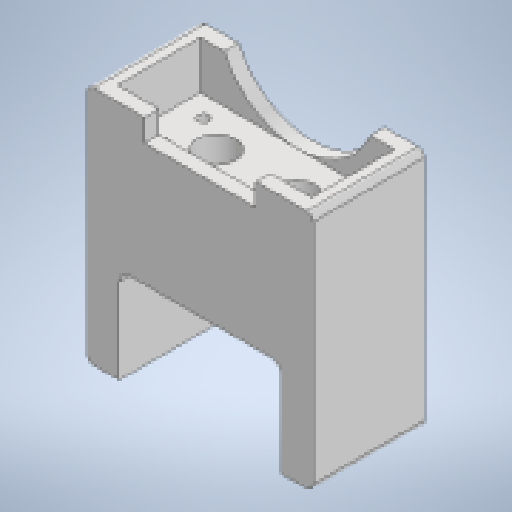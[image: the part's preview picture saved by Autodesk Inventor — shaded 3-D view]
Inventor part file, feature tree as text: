
AUTODESK INVENTOR PART (.ipt)
format: ipt  version: 2023 (Build 270158000, 158)  size: 233,472 bytes
history: native  units: in
note: dims shown in document units (in); Inventor stores cm internally (conversion verified against a paired STEP export)
features: extrude x8, sketch x7, fillet x2
ambient origin geometry x8: Origin, YZ Plane, XZ Plane, XY Plane, X Axis, Y Axis, Z Axis, Center Point
bodies: Solid1 (feature_tree)
feature tree (17):
  sketch  "Sketch1"  dims[d0=0.9843in d1=2.3622in]
  extrude  "Extrusion1"  Depth=0.9843in
  extrude  "Extrusion2"  Depth=0.0197in
  extrude  "Extrusion3"  Depth=0.0197in
  extrude  "Extrusion4"  Depth=1.811in
  extrude  "Extrusion5"  Depth=2.7874in
  extrude  "Extrusion6"  Depth=0.3937in TaperAngle=0.0deg
  fillet  "Fillet1"  Radius=1.3937in
  fillet  "Fillet2"  Radius=0.3937in
  extrude  "Extrusion7"  Depth=2.0in
  extrude  "Extrusion8"  Depth=0.125in
  sketch  "Sketch2"  dims[d2=0.0197in d3=0.0197in]
  sketch  "Sketch3"  dims[d4=0.0197in d5=0.0197in]
  sketch  "Sketch4"  dims[d6=0.1417in d7=1.811in]
  sketch  "Sketch5"  dims[d8=0.5118in d9=2.7874in]
  sketch  "Sketch6"  dims[d10=1.378in d11=0.3937in d12=0.0in d13=1.3937in d14=0.0in]
  sketch  "Sketch7"  dims[d15=0.3937in d16=0.1969in d17=0.0in d18=0.0in d19=0.3937in d20=1.1969in d21=0.0in d22=0.0in d23=2.0in d24=0.125in d25=0.3937in d26=1.1811in d27=0.3937in d28=0.0in d29=0.2362in d30=0.9843in d31=0.3937in d32=0.0in d34=0.4724in d35=0.3937in d36=0.0in d37=0.0787in d38=0.0787in d39=1.5118in d40=1.378in d41=2.0812in d42=0.0in d44=0.9843in d45=0.3937in d46=0.3937in d47=0.0in]
